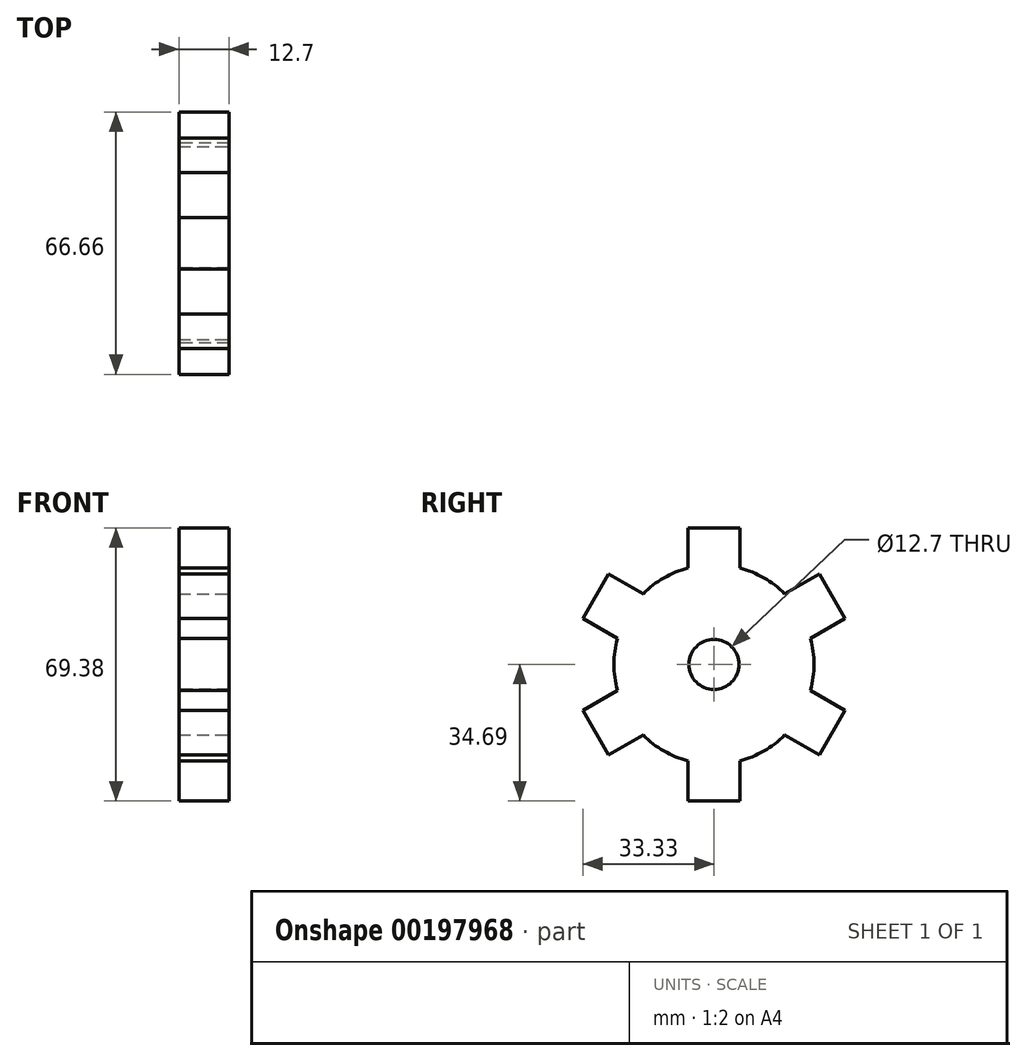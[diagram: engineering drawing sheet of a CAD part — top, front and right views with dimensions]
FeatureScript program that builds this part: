
annotation { "Feature Type Name" : "Feature", "Feature Type Description" : "" }
export const myFeature = defineFeature(function(context is Context, id is Id, definition is map)
    precondition{}
    {
        {
            var Q0;
            Q0=qCreatedBy(makeId("Right.planeOp"),FACE);
            var sketch = newSketch(context, id + "F0", { "sketchPlane" : qUnion([Q0])});
            skCircle(sketch, "E0", {"center": v(0, 0) * mm, "radius": 25.4 * mm});
            skSolve(sketch);
        }
        {
            var Q0;
            Q0 = qSketchRegion(id + "F0", true);
            var Q1;
            Q1 = qSketchRegion(id + "F2", true);
            extrude(context, id + "F1", {"entities" : qUnion([Q0, Q1]), "endBound" : BoundingType.SYMMETRIC, "depth" : 12.7 * mm});
        }
        {
            var Q0;
            Q0=makeQuery(id+"F1.opExtrude","CAP_FACE",FACE,{"disambiguationData":[OSD([sQuery(id+"F0.wireOp",EDGE,"E0")])],"isStart":false});
            var sketch = newSketch(context, id + "F2", { "sketchPlane" : qUnion([Q0])});
            skLineSegment(sketch, "E1", {"start": v(0, 0) * mm, "end": v(0, -25.4) * mm});
            skLineSegment(sketch, "E2", {"start": v(0, 0) * mm, "end": v(-6.57, -24.53) * mm});
            skLineSegment(sketch, "E3", {"start": v(0, 0) * mm, "end": v(6.57, -24.53) * mm});
            skLineSegment(sketch, "E4", {"start": v(6.57, -24.53) * mm, "end": v(-6.57, -24.53) * mm});
            skLineSegment(sketch, "E5.0", {"start": v(6.57, -34.7) * mm, "end": v(-6.57, -34.7) * mm});
            skLineSegment(sketch, "E6", {"start": v(6.57, -34.7) * mm, "end": v(6.57, -24.53) * mm});
            skLineSegment(sketch, "E7", {"start": v(-6.57, -34.7) * mm, "end": v(-6.57, -24.53) * mm});
            skSolve(sketch);
        }
        {
            var Q0;
            Q0 = qSketchRegion(id + "F2", true);
            extrude(context, id + "F3", {"entities" : qUnion([Q0]), "operationType" : NewBodyOperationType.ADD, "oppositeDirection" : true, "depth" : 12.7 * mm});
        }
        {
            var Q0;
            Q0=qCreatedBy(makeId("Top.planeOp"),FACE);
            var sketch = newSketch(context, id + "F4", { "sketchPlane" : qUnion([Q0])});
            skLineSegment(sketch, "E8", {"start": v(0, 0) * mm, "end": v(50.08, 0) * mm});
            skSolve(sketch);
        }
        {
            var Q0;
            Q0=makeQuery(id+"F1.opExtrude","SWEPT_BODY",BODY,{"disambiguationData":[OSD([sQuery(id+"F0.wireOp",EDGE,"E0")])]});
            var Q1;
            Q1=sQuery(id+"F4.wireOp",EDGE,"E8");
            circularPattern(context, id + "F5", {"operationType" : NewBodyOperationType.ADD, "entities" : qUnion([Q0]), "axis" : qUnion([Q1]), "angle" : 360 * degree, "instanceCount" : 6, "equalSpace" : true});
        }
        {
            var Q0;
            {var subQ0=makeQuery(id+"F3.boolean.opBoolean","MERGE",FACE,{"derivedFrom":[makeQuery(id+"F1.opExtrude","CAP_FACE",FACE,{"disambiguationData":[OSD([sQuery(id+"F0.wireOp",EDGE,"E0")])],"isStart":true}),makeQuery(id+"F3.opExtrude","CAP_FACE",FACE,{"disambiguationData":[OSD([sQuery(id+"F2.wireOp",EDGE,"E2"),sQuery(id+"F2.wireOp",EDGE,"E3"),sQuery(id+"F2.wireOp",EDGE,"E5.0"),sQuery(id+"F2.wireOp",EDGE,"E6"),sQuery(id+"F2.wireOp",EDGE,"E7")])],"isStart":false})]});Q0=makeQuery(id+"F5.boolean.opBoolean","MERGE",FACE,{"derivedFrom":[subQ0,makeQuery(id+"F5.opPattern","COPY",FACE,{"derivedFrom":subQ0,"instanceName":"1"}),makeQuery(id+"F5.opPattern","COPY",FACE,{"derivedFrom":subQ0,"instanceName":"2"}),makeQuery(id+"F5.opPattern","COPY",FACE,{"derivedFrom":subQ0,"instanceName":"3"}),makeQuery(id+"F5.opPattern","COPY",FACE,{"derivedFrom":subQ0,"instanceName":"4"}),makeQuery(id+"F5.opPattern","COPY",FACE,{"derivedFrom":subQ0,"instanceName":"5"})]});}
            var sketch = newSketch(context, id + "F6", { "sketchPlane" : qUnion([Q0])});
            skCircle(sketch, "E9", {"center": v(0, 0) * mm, "radius": 6.35 * mm});
            skSolve(sketch);
        }
        {
            var Q0;
            Q0=makeQuery(id+"F6.imprint","IMPRINT",FACE,{"disambiguationData":[TD([[makeQuery(id+"F6.imprint","IMPRINT",EDGE,{"derivedFrom":sQuery(id+"F6.wireOp",EDGE,"E9")}),1.0]])]});
            extrude(context, id + "F7", {"entities" : qUnion([Q0]), "operationType" : NewBodyOperationType.REMOVE, "oppositeDirection" : true, "depth" : 25.4 * mm});
        }
    });
